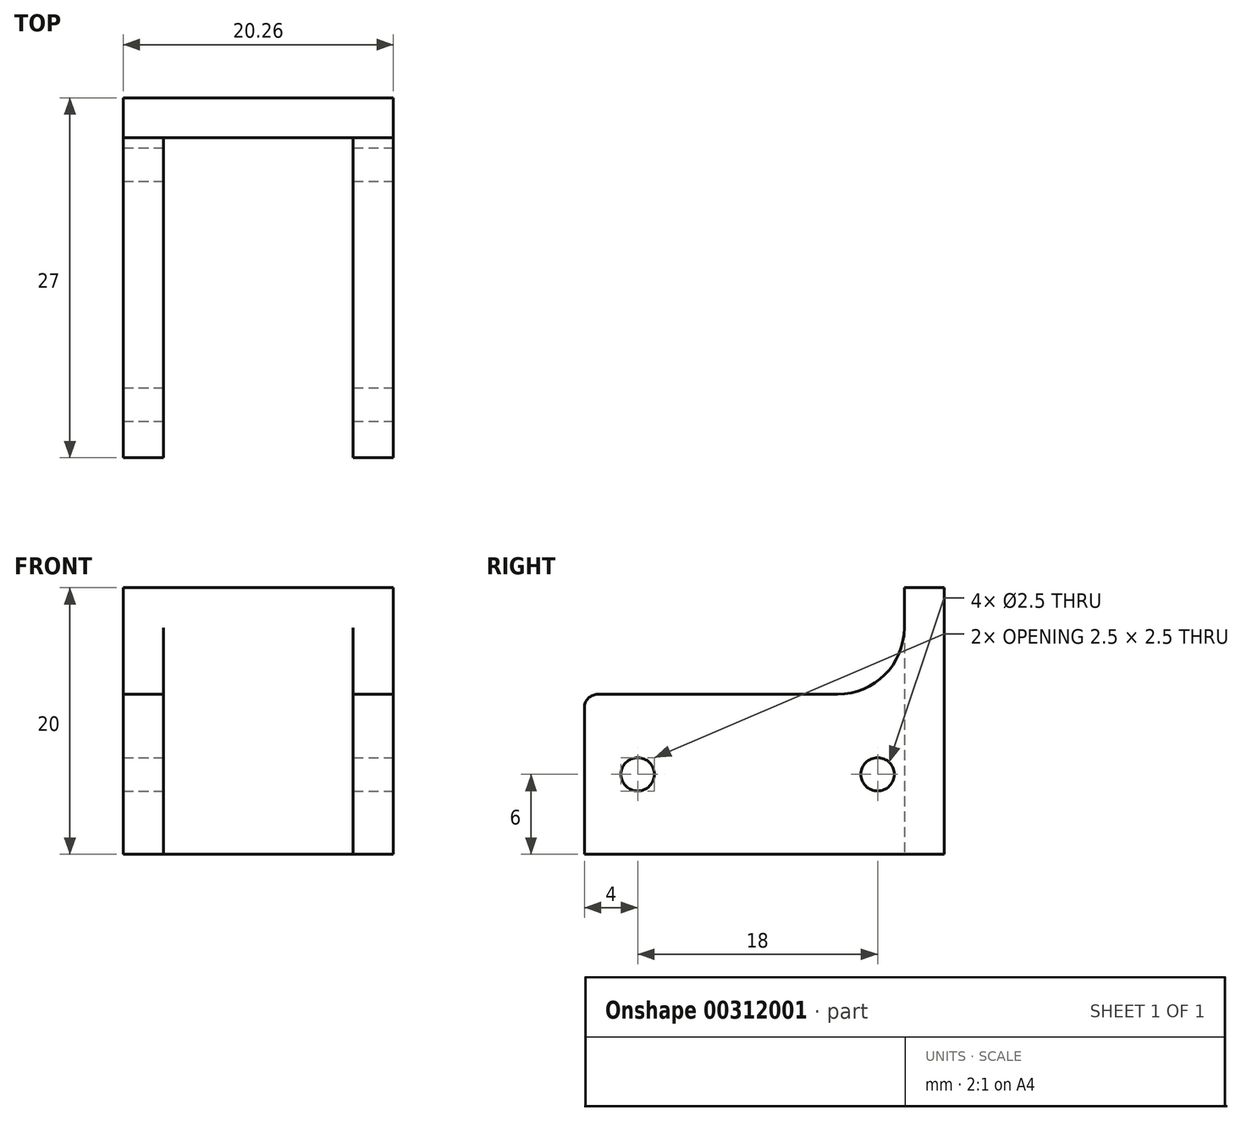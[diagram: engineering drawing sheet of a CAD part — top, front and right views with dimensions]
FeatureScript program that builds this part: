
annotation { "Feature Type Name" : "Feature", "Feature Type Description" : "" }
export const myFeature = defineFeature(function(context is Context, id is Id, definition is map)
    precondition{}
    {
        {
            var Q0;
            Q0=qCreatedBy(makeId("Top.planeOp"),FACE);
            var sketch = newSketch(context, id + "F0", { "sketchPlane" : qUnion([Q0])});
            skLineSegment(sketch, "E0.bottom", {"start": v(-10.12, 13.5) * mm, "end": v(10.13, 13.5) * mm});
            skLineSegment(sketch, "E0.top", {"start": v(-10.13, -13.5) * mm, "end": v(10.12, -13.5) * mm});
            skLineSegment(sketch, "E0.left", {"start": v(-10.12, 13.5) * mm, "end": v(-10.13, -13.5) * mm});
            skLineSegment(sketch, "E0.right", {"start": v(10.13, 13.5) * mm, "end": v(10.12, -13.5) * mm});
            skPoint(sketch, "E0.middle", {"position": v(0, 0) * mm});
            skLineSegment(sketch, "E1.bottom", {"start": v(7.12, -13.5) * mm, "end": v(-7.13, -13.5) * mm});
            skLineSegment(sketch, "E1.top", {"start": v(10.13, 10.5) * mm, "end": v(-10.12, 10.5) * mm});
            skLineSegment(sketch, "E1.left", {"start": v(7.12, -13.5) * mm, "end": v(7.13, 10.5) * mm});
            skLineSegment(sketch, "E1.right", {"start": v(-7.13, -13.5) * mm, "end": v(-7.12, 10.5) * mm});
            skSolve(sketch);
        }
        {
            var Q0;
            {var subQ3=sQuery(id+"F0.wireOp",EDGE,"E1.left");Q0=makeQuery(id+"F0.imprint","IMPRINT",FACE,{"disambiguationData":[TD([[makeQuery(id+"F0.imprint","IMPRINT",EDGE,{"derivedFrom":subQ3}),-1.0]])]});}
            var Q1;
            {var subQ3=sQuery(id+"F0.wireOp",EDGE,"E1.right");Q1=makeQuery(id+"F0.imprint","IMPRINT",FACE,{"disambiguationData":[TD([[makeQuery(id+"F0.imprint","IMPRINT",EDGE,{"derivedFrom":subQ3}),1.0]])]});}
            var Q2;
            {var subQ5=sQuery(id+"F0.wireOp",EDGE,"E0.bottom");Q2=makeQuery(id+"F0.imprint","IMPRINT",FACE,{"disambiguationData":[TD([[makeQuery(id+"F0.imprint","IMPRINT",EDGE,{"derivedFrom":subQ5}),-1.0]])]});}
            var Q3;
            {var subQ3=sQuery(id+"F0.wireOp",EDGE,"765ba905-0b8b-4cfc-8a0b-93087641a54d5.MirrorCS");Q3=makeQuery(id+"F0.imprint","IMPRINT",FACE,{"disambiguationData":[TD([[makeQuery(id+"F0.imprint","IMPRINT",EDGE,{"derivedFrom":subQ3}),1.0]])]});}
            var Q4;
            {var subQ3=sQuery(id+"F0.wireOp",EDGE,"765ba905-0b8b-4cfc-8a0b-93087641a54d6.MirrorCS");Q4=makeQuery(id+"F0.imprint","IMPRINT",FACE,{"disambiguationData":[TD([[makeQuery(id+"F0.imprint","IMPRINT",EDGE,{"derivedFrom":subQ3}),-1.0]])]});}
            var Q5;
            {var subQ0=sQuery(id+"F0.wireOp",EDGE,"lA1S6t7q-6HNF-ZRqw-uof4-38xPiZ8Q4yXE");Q5=makeQuery(id+"F0.imprint","IMPRINT",FACE,{"disambiguationData":[TD([[makeQuery(id+"F0.imprint","IMPRINT",EDGE,{"derivedFrom":subQ0}),-1.0]])]});}
            var Q6;
            {var subQ2=sQuery(id+"F0.wireOp",EDGE,"765ba905-0b8b-4cfc-8a0b-93087641a54d1.MirrorCS");var subQ7=sQuery(id+"F0.wireOp",EDGE,"765ba905-0b8b-4cfc-8a0b-93087641a54d8.MirrorCS");var subQ8=makeQuery(id+"F0.imprint","INTERSECT",VERTEX,{"derivedFrom":[subQ2,subQ7]});Q6=makeQuery(id+"F0.imprint","IMPRINT",FACE,{"disambiguationData":[TD([[makeQuery(id+"F0.imprint","IMPRINT",EDGE,{"disambiguationData":[TD([[subQ8,-1.0]])],"derivedFrom":subQ2}),-1.0]])]});}
            var Q7;
            {var subQ1=sQuery(id+"F0.wireOp",EDGE,"E0.right");var subQ5=sQuery(id+"F0.wireOp",EDGE,"E0.bottom");var subQ8=makeQuery(id+"F0.imprint","INTERSECT",VERTEX,{"derivedFrom":[subQ5,subQ1]});Q7=makeQuery(id+"F0.imprint","IMPRINT",FACE,{"disambiguationData":[TD([[makeQuery(id+"F0.imprint","IMPRINT",EDGE,{"disambiguationData":[TD([[subQ8,1.0]])],"derivedFrom":subQ5}),-1.0]])]});}
            extrude(context, id + "F1", {"entities" : qUnion([Q0, Q1, Q2, Q3, Q4, Q5, Q6, Q7]), "depth" : 12 * mm});
        }
        {
            var Q0;
            Q0=makeQuery(id+"F1.opExtrude","SWEPT_FACE",FACE,{"disambiguationData":[OSD([sQuery(id+"F0.wireOp",EDGE,"E0.right")])]});
            var sketch = newSketch(context, id + "F2", { "sketchPlane" : qUnion([Q0])});
            skCircle(sketch, "E2", {"center": v(-9.5, 6) * mm, "radius": 1.25 * mm});
            skPoint(sketch, "E2.centerSnap0", {"position": v(-13.5, 6) * mm});
            skPoint(sketch, "E3.centerSnap0", {"position": v(13.5, 6) * mm});
            skLineSegment(sketch, "E4.0", {"start": v(10.5, 12) * mm, "end": v(10.5, 0) * mm});
            skCircle(sketch, "E5", {"center": v(8.5, 6) * mm, "radius": 1.25 * mm});
            skLineSegment(sketch, "E6", {"start": v(-0.5, 23) * mm, "end": v(-0.5, 0) * mm, "construction": true});
            skCircle(sketch, "E7", {"center": v(-0.5, 14.45) * mm, "radius": 4.65 * mm});
            skLineSegment(sketch, "E8", {"start": v(-9.5, 6) * mm, "end": v(8.5, 6) * mm, "construction": true});
            skLineSegment(sketch, "E9", {"start": v(4.15, 14.45) * mm, "end": v(-0.18, 14.45) * mm});
            skLineSegment(sketch, "E10", {"start": v(-12.82, 14.45) * mm, "end": v(-13.5, 0) * mm});
            skSolve(sketch);
        }
        {
            var Q0;
            Q0=makeQuery(id+"F2.imprint","IMPRINT",FACE,{"disambiguationData":[TD([[makeQuery(id+"F2.imprint","IMPRINT",EDGE,{"derivedFrom":sQuery(id+"F2.wireOp",EDGE,"E2")}),1.0]])]});
            var Q1;
            Q1=makeQuery(id+"F2.imprint","IMPRINT",FACE,{"disambiguationData":[TD([[makeQuery(id+"F2.imprint","IMPRINT",EDGE,{"derivedFrom":sQuery(id+"F2.wireOp",EDGE,"E5")}),1.0]])]});
            extrude(context, id + "F3", {"entities" : qUnion([Q0, Q1]), "operationType" : NewBodyOperationType.REMOVE, "oppositeDirection" : true, "depth" : 150 * mm});
        }
        {
            var Q0;
            {var subQ5=sQuery(id+"F0.wireOp",EDGE,"E0.bottom");Q0=makeQuery(id+"F0.imprint","IMPRINT",FACE,{"disambiguationData":[TD([[makeQuery(id+"F0.imprint","IMPRINT",EDGE,{"derivedFrom":subQ5}),-1.0]])]});}
            var Q1;
            {var subQ0=sQuery(id+"F0.wireOp",EDGE,"lA1S6t7q-6HNF-ZRqw-uof4-38xPiZ8Q4yXE");Q1=makeQuery(id+"F0.imprint","IMPRINT",FACE,{"disambiguationData":[TD([[makeQuery(id+"F0.imprint","IMPRINT",EDGE,{"derivedFrom":subQ0}),-1.0]])]});}
            var Q2;
            {var subQ2=sQuery(id+"F0.wireOp",EDGE,"765ba905-0b8b-4cfc-8a0b-93087641a54d1.MirrorCS");var subQ7=sQuery(id+"F0.wireOp",EDGE,"765ba905-0b8b-4cfc-8a0b-93087641a54d8.MirrorCS");var subQ8=makeQuery(id+"F0.imprint","INTERSECT",VERTEX,{"derivedFrom":[subQ2,subQ7]});Q2=makeQuery(id+"F0.imprint","IMPRINT",FACE,{"disambiguationData":[TD([[makeQuery(id+"F0.imprint","IMPRINT",EDGE,{"disambiguationData":[TD([[subQ8,-1.0]])],"derivedFrom":subQ2}),-1.0]])]});}
            var Q3;
            {var subQ1=sQuery(id+"F0.wireOp",EDGE,"E0.right");var subQ5=sQuery(id+"F0.wireOp",EDGE,"E0.bottom");var subQ8=makeQuery(id+"F0.imprint","INTERSECT",VERTEX,{"derivedFrom":[subQ5,subQ1]});Q3=makeQuery(id+"F0.imprint","IMPRINT",FACE,{"disambiguationData":[TD([[makeQuery(id+"F0.imprint","IMPRINT",EDGE,{"disambiguationData":[TD([[subQ8,1.0]])],"derivedFrom":subQ5}),-1.0]])]});}
            extrude(context, id + "F4", {"entities" : qUnion([Q0, Q1, Q2, Q3]), "operationType" : NewBodyOperationType.ADD, "depth" : 20 * mm});
        }
        {
            var Q0;
            {var subQ0=sQuery(id+"F0.wireOp",EDGE,"E1.top");Q0=makeQuery(id+"F4.boolean.opBoolean","INTERSECT",EDGE,{"disambiguationData":[OD(1.0)],"derivedFrom":[makeQuery(id+"F1.opExtrude","CAP_FACE",FACE,{"disambiguationData":[OSD([sQuery(id+"F0.wireOp",EDGE,"E0.bottom"),sQuery(id+"F0.wireOp",EDGE,"E0.top"),sQuery(id+"F0.wireOp",EDGE,"E0.left"),sQuery(id+"F0.wireOp",EDGE,"E0.right"),subQ0,sQuery(id+"F0.wireOp",EDGE,"E1.left"),sQuery(id+"F0.wireOp",EDGE,"E1.right")])],"isStart":false}),makeQuery(id+"F4.opExtrude","SWEPT_FACE",FACE,{"disambiguationData":[OSD([subQ0])]})]});}
            var Q1;
            {var subQ0=sQuery(id+"F0.wireOp",EDGE,"E1.top");Q1=makeQuery(id+"F4.boolean.opBoolean","INTERSECT",EDGE,{"disambiguationData":[OD(0.0)],"derivedFrom":[makeQuery(id+"F1.opExtrude","CAP_FACE",FACE,{"disambiguationData":[OSD([sQuery(id+"F0.wireOp",EDGE,"E0.bottom"),sQuery(id+"F0.wireOp",EDGE,"E0.top"),sQuery(id+"F0.wireOp",EDGE,"E0.left"),sQuery(id+"F0.wireOp",EDGE,"E0.right"),subQ0,sQuery(id+"F0.wireOp",EDGE,"E1.left"),sQuery(id+"F0.wireOp",EDGE,"E1.right")])],"isStart":false}),makeQuery(id+"F4.opExtrude","SWEPT_FACE",FACE,{"disambiguationData":[OSD([subQ0])]})]});}
            var Q2;
            {var subQ0=sQuery(id+"F0.wireOp",EDGE,"765ba905-0b8b-4cfc-8a0b-93087641a54d2.MirrorCS");var subQ1=sQuery(id+"F0.wireOp",EDGE,"E1.top");Q2=makeQuery(id+"F4.boolean.opBoolean","INTERSECT",EDGE,{"disambiguationData":[OD(2.0)],"derivedFrom":[makeQuery(id+"F1.opExtrude","CAP_FACE",FACE,{"disambiguationData":[OSD([sQuery(id+"F0.wireOp",EDGE,"E0.bottom"),sQuery(id+"F0.wireOp",EDGE,"E0.top"),sQuery(id+"F0.wireOp",EDGE,"E0.left"),sQuery(id+"F0.wireOp",EDGE,"E0.right"),subQ1,sQuery(id+"F0.wireOp",EDGE,"E1.left"),sQuery(id+"F0.wireOp",EDGE,"E1.right"),sQuery(id+"F0.wireOp",EDGE,"765ba905-0b8b-4cfc-8a0b-93087641a54d0.MirrorCS"),sQuery(id+"F0.wireOp",EDGE,"765ba905-0b8b-4cfc-8a0b-93087641a54d1.MirrorCS"),subQ0,sQuery(id+"F0.wireOp",EDGE,"765ba905-0b8b-4cfc-8a0b-93087641a54d4.MirrorCS"),sQuery(id+"F0.wireOp",EDGE,"765ba905-0b8b-4cfc-8a0b-93087641a54d5.MirrorCS"),sQuery(id+"F0.wireOp",EDGE,"765ba905-0b8b-4cfc-8a0b-93087641a54d6.MirrorCS"),sQuery(id+"F0.wireOp",EDGE,"765ba905-0b8b-4cfc-8a0b-93087641a54d8.MirrorCS")])],"isStart":false}),makeQuery(id+"F4.opExtrude","SWEPT_FACE",FACE,{"disambiguationData":[OSD([subQ1,subQ0])]})]});}
            var Q3;
            {var subQ0=sQuery(id+"F0.wireOp",EDGE,"765ba905-0b8b-4cfc-8a0b-93087641a54d2.MirrorCS");var subQ1=sQuery(id+"F0.wireOp",EDGE,"E1.top");Q3=makeQuery(id+"F4.boolean.opBoolean","INTERSECT",EDGE,{"disambiguationData":[OD(3.0)],"derivedFrom":[makeQuery(id+"F1.opExtrude","CAP_FACE",FACE,{"disambiguationData":[OSD([sQuery(id+"F0.wireOp",EDGE,"E0.bottom"),sQuery(id+"F0.wireOp",EDGE,"E0.top"),sQuery(id+"F0.wireOp",EDGE,"E0.left"),sQuery(id+"F0.wireOp",EDGE,"E0.right"),subQ1,sQuery(id+"F0.wireOp",EDGE,"E1.left"),sQuery(id+"F0.wireOp",EDGE,"E1.right"),sQuery(id+"F0.wireOp",EDGE,"765ba905-0b8b-4cfc-8a0b-93087641a54d0.MirrorCS"),sQuery(id+"F0.wireOp",EDGE,"765ba905-0b8b-4cfc-8a0b-93087641a54d1.MirrorCS"),subQ0,sQuery(id+"F0.wireOp",EDGE,"765ba905-0b8b-4cfc-8a0b-93087641a54d4.MirrorCS"),sQuery(id+"F0.wireOp",EDGE,"765ba905-0b8b-4cfc-8a0b-93087641a54d5.MirrorCS"),sQuery(id+"F0.wireOp",EDGE,"765ba905-0b8b-4cfc-8a0b-93087641a54d6.MirrorCS"),sQuery(id+"F0.wireOp",EDGE,"765ba905-0b8b-4cfc-8a0b-93087641a54d8.MirrorCS")])],"isStart":false}),makeQuery(id+"F4.opExtrude","SWEPT_FACE",FACE,{"disambiguationData":[OSD([subQ1,subQ0])]})]});}
            fillet(context, id + "F5", {"entities" : qUnion([Q0, Q1, Q2, Q3]), "radius" : 5 * mm, "tangentPropagation" : true, "allowEdgeOverflow" : false});
        }
        {
            var Q0;
            {var subQ0=sQuery(id+"F0.wireOp",EDGE,"E0.top");Q0=makeQuery(id+"F1.opExtrude","CAP_EDGE",EDGE,{"disambiguationData":[OSD([subQ0]),TDD([makeQuery(id+"F0.imprint","IMPRINT",EDGE,{"disambiguationData":[TD([[makeQuery(id+"F0.imprint","INTERSECT",VERTEX,{"derivedFrom":[subQ0,sQuery(id+"F0.wireOp",EDGE,"E0.right")]}),1.0]])],"derivedFrom":subQ0})])],"isStart":false});}
            var Q1;
            {var subQ0=sQuery(id+"F0.wireOp",EDGE,"E0.top");Q1=makeQuery(id+"F1.opExtrude","CAP_EDGE",EDGE,{"disambiguationData":[OSD([subQ0]),TDD([makeQuery(id+"F0.imprint","IMPRINT",EDGE,{"disambiguationData":[TD([[makeQuery(id+"F0.imprint","INTERSECT",VERTEX,{"derivedFrom":[subQ0,sQuery(id+"F0.wireOp",EDGE,"E0.left")]}),-1.0]])],"derivedFrom":subQ0})])],"isStart":false});}
            var Q2;
            {var subQ0=sQuery(id+"F0.wireOp",EDGE,"765ba905-0b8b-4cfc-8a0b-93087641a54d0.MirrorCS");Q2=makeQuery(id+"F1.opExtrude","CAP_EDGE",EDGE,{"disambiguationData":[OSD([subQ0]),TDD([makeQuery(id+"F0.imprint","IMPRINT",EDGE,{"disambiguationData":[TD([[makeQuery(id+"F0.imprint","INTERSECT",VERTEX,{"derivedFrom":[subQ0,sQuery(id+"F0.wireOp",EDGE,"765ba905-0b8b-4cfc-8a0b-93087641a54d4.MirrorCS")]}),1.0]])],"derivedFrom":subQ0})])],"isStart":false});}
            var Q3;
            {var subQ0=sQuery(id+"F0.wireOp",EDGE,"765ba905-0b8b-4cfc-8a0b-93087641a54d0.MirrorCS");Q3=makeQuery(id+"F1.opExtrude","CAP_EDGE",EDGE,{"disambiguationData":[OSD([subQ0]),TDD([makeQuery(id+"F0.imprint","IMPRINT",EDGE,{"disambiguationData":[TD([[makeQuery(id+"F0.imprint","INTERSECT",VERTEX,{"derivedFrom":[subQ0,sQuery(id+"F0.wireOp",EDGE,"765ba905-0b8b-4cfc-8a0b-93087641a54d1.MirrorCS")]}),-1.0]])],"derivedFrom":subQ0})])],"isStart":false});}
            fillet(context, id + "F6", {"entities" : qUnion([Q0, Q1, Q2, Q3]), "radius" : 1 * mm, "tangentPropagation" : true, "allowEdgeOverflow" : false});
        }
        {
            var Q0;
            {var subQ0=sQuery(id+"F2.wireOp",EDGE,"E7");var subQ1=makeQuery(id+"F1.opExtrude","CAP_EDGE",EDGE,{"disambiguationData":[OSD([sQuery(id+"F0.wireOp",EDGE,"E0.right")])],"isStart":false});var subQ2=makeQuery(id+"F2.imprint","INTERSECT",VERTEX,{"disambiguationData":[OD(0.0)],"derivedFrom":[subQ1,subQ0]});Q0=makeQuery(id+"F2.imprint","IMPRINT",FACE,{"disambiguationData":[TD([[makeQuery(id+"F2.imprint","IMPRINT",EDGE,{"disambiguationData":[TD([[subQ2,-1.0]])],"derivedFrom":subQ0}),1.0]])]});}
            var Q1;
            {var subQ0=sQuery(id+"F2.wireOp",EDGE,"E7");var subQ1=makeQuery(id+"F2.imprint","IMPRINT",VERTEX,{"derivedFrom":subQ0});Q1=makeQuery(id+"F2.imprint","IMPRINT",FACE,{"disambiguationData":[TD([[makeQuery(id+"F2.imprint","IMPRINT",EDGE,{"disambiguationData":[TD([[subQ1,-1.0]])],"derivedFrom":subQ0}),1.0]])]});}
            extrude(context, id + "F7", {"entities" : qUnion([Q0, Q1]), "operationType" : NewBodyOperationType.REMOVE, "oppositeDirection" : true, "depth" : 150 * mm});
        }
    });
